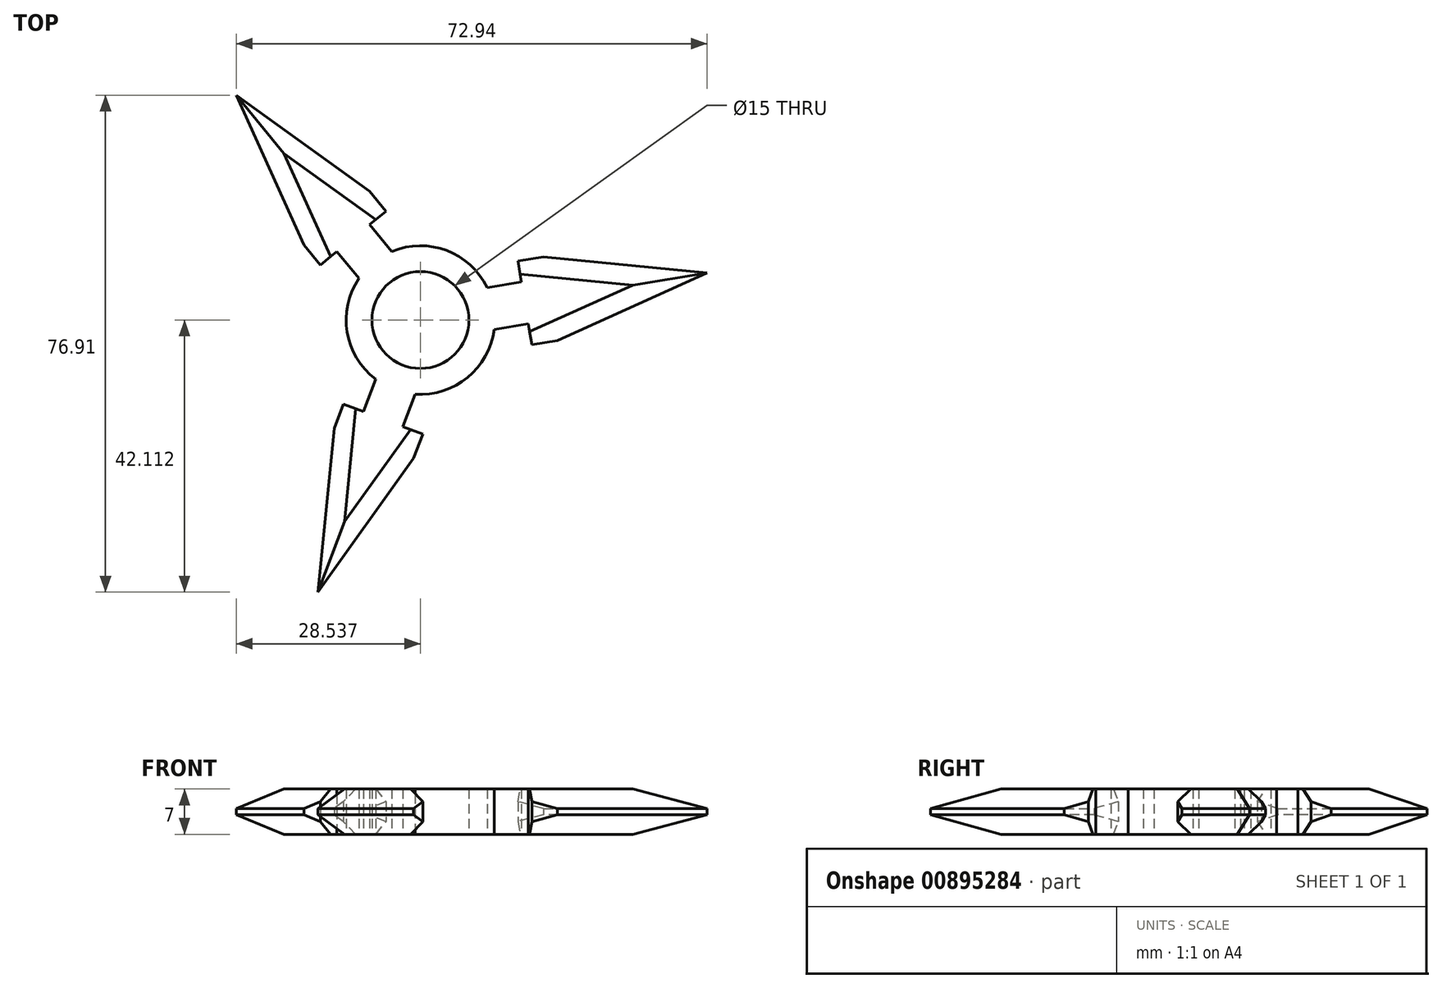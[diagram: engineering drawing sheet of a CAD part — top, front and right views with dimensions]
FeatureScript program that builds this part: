
annotation { "Feature Type Name" : "Feature", "Feature Type Description" : "" }
export const myFeature = defineFeature(function(context is Context, id is Id, definition is map)
    precondition{}
    {
        {
            var Q0;
            Q0=qCreatedBy(makeId("Top.planeOp"),FACE);
            var sketch = newSketch(context, id + "F0", { "sketchPlane" : qUnion([Q0])});
            skLineSegment(sketch, "E0", {"start": v(-19.22, 0.26) * mm, "end": v(-22.63, 4.41) * mm});
            skLineSegment(sketch, "E1", {"start": v(-22.63, 4.41) * mm, "end": v(-25.16, 2.34) * mm});
            skPoint(sketch, "E1.endSnap0", {"position": v(-20.92, 2.34) * mm});
            skLineSegment(sketch, "E2", {"start": v(-25.16, 2.34) * mm, "end": v(-27.7, 5.43) * mm});
            skLineSegment(sketch, "E3", {"start": v(-27.7, 5.43) * mm, "end": v(-38.23, 28.6) * mm});
            skLineSegment(sketch, "E4", {"start": v(-38.23, 28.6) * mm, "end": v(-17.56, 13.75) * mm});
            skLineSegment(sketch, "E5", {"start": v(-17.56, 13.75) * mm, "end": v(-15.02, 10.65) * mm});
            skLineSegment(sketch, "E6", {"start": v(-15.02, 10.65) * mm, "end": v(-17.56, 8.57) * mm});
            skLineSegment(sketch, "E7", {"start": v(-17.56, 8.57) * mm, "end": v(-14.15, 4.41) * mm});
            skCircle(sketch, "E8", {"center": v(-9.7, -6.19) * mm, "radius": 11.5 * mm});
            skLineSegment(sketch, "E9.1.0", {"start": v(-25.56, -48.3) * mm, "end": v(-23.03, -22.97) * mm});
            skLineSegment(sketch, "E9.1.1", {"start": v(-10.75, -27.6) * mm, "end": v(-25.56, -48.3) * mm});
            skLineSegment(sketch, "E9.1.2", {"start": v(-9.34, -23.85) * mm, "end": v(-10.75, -27.6) * mm});
            skLineSegment(sketch, "E9.1.3", {"start": v(-12.4, -22.7) * mm, "end": v(-9.34, -23.85) * mm});
            skLineSegment(sketch, "E9.1.4", {"start": v(-10.51, -17.66) * mm, "end": v(-12.4, -22.7) * mm});
            skLineSegment(sketch, "E9.1.5", {"start": v(-18.55, -20.38) * mm, "end": v(-16.65, -15.35) * mm});
            skLineSegment(sketch, "E9.1.6", {"start": v(-21.62, -19.22) * mm, "end": v(-18.55, -20.38) * mm});
            skLineSegment(sketch, "E9.1.7", {"start": v(-23.03, -22.97) * mm, "end": v(-21.62, -19.22) * mm});
            skLineSegment(sketch, "E9.2.0", {"start": v(34.7, 1.12) * mm, "end": v(11.5, -9.35) * mm});
            skLineSegment(sketch, "E9.2.1", {"start": v(9.37, 3.6) * mm, "end": v(34.7, 1.12) * mm});
            skLineSegment(sketch, "E9.2.2", {"start": v(5.42, 2.95) * mm, "end": v(9.37, 3.6) * mm});
            skLineSegment(sketch, "E9.2.3", {"start": v(5.96, -0.29) * mm, "end": v(5.42, 2.95) * mm});
            skLineSegment(sketch, "E9.2.4", {"start": v(0.65, -1.16) * mm, "end": v(5.96, -0.29) * mm});
            skLineSegment(sketch, "E9.2.5", {"start": v(7.02, -6.76) * mm, "end": v(1.72, -7.63) * mm});
            skLineSegment(sketch, "E9.2.6", {"start": v(7.56, -10) * mm, "end": v(7.02, -6.76) * mm});
            skLineSegment(sketch, "E9.2.7", {"start": v(11.5, -9.35) * mm, "end": v(7.56, -10) * mm});
            skLineSegment(sketch, "E10", {"start": v(-25.56, -48.3) * mm, "end": v(-9.7, -6.19) * mm, "construction": true});
            skCircle(sketch, "E11", {"center": v(-9.7, -6.19) * mm, "radius": 7.5 * mm});
            skCircle(sketch, "E12", {"center": v(-9.7, -6.19) * mm, "radius": 45 * mm, "construction": true});
            skSolve(sketch);
        }
        {
            var Q0;
            Q0=makeQuery(id+"F0.imprint","IMPRINT",FACE,{"disambiguationData":[TD([[makeQuery(id+"F0.imprint","IMPRINT",EDGE,{"derivedFrom":sQuery(id+"F0.wireOp",EDGE,"E9.1.0")}),-1.0]])]});
            var Q1;
            Q1=makeQuery(id+"F0.imprint","IMPRINT",FACE,{"disambiguationData":[TD([[makeQuery(id+"F0.imprint","IMPRINT",EDGE,{"derivedFrom":sQuery(id+"F0.wireOp",EDGE,"E9.2.0")}),-1.0]])]});
            var Q2;
            {var subQ0=sQuery(id+"F0.wireOp",EDGE,"E0");Q2=makeQuery(id+"F0.imprint","IMPRINT",FACE,{"disambiguationData":[TD([[makeQuery(id+"F0.imprint","IMPRINT",EDGE,{"derivedFrom":subQ0}),-1.0]])]});}
            var Q3;
            {var subQ5=sQuery(id+"F0.wireOp",EDGE,"E1");Q3=makeQuery(id+"F0.imprint","IMPRINT",FACE,{"disambiguationData":[TD([[makeQuery(id+"F0.imprint","IMPRINT",EDGE,{"derivedFrom":subQ5}),-1.0]])]});}
            var Q4;
            {var subQ0=sQuery(id+"F0.wireOp",EDGE,"E8");var subQ1=sQuery(id+"F0.wireOp",EDGE,"E7");var subQ2=makeQuery(id+"F0.imprint","INTERSECT",VERTEX,{"derivedFrom":[subQ1,subQ0]});Q4=makeQuery(id+"F0.imprint","IMPRINT",FACE,{"disambiguationData":[TD([[makeQuery(id+"F0.imprint","IMPRINT",EDGE,{"disambiguationData":[TD([[subQ2,1.0]])],"derivedFrom":subQ1}),1.0]])]});}
            var Q5;
            {var subQ0=sQuery(id+"F0.wireOp",EDGE,"E8");var subQ1=sQuery(id+"F0.wireOp",EDGE,"E0");var subQ2=makeQuery(id+"F0.imprint","INTERSECT",VERTEX,{"derivedFrom":[subQ1,subQ0]});Q5=makeQuery(id+"F0.imprint","IMPRINT",FACE,{"disambiguationData":[TD([[makeQuery(id+"F0.imprint","IMPRINT",EDGE,{"disambiguationData":[TD([[subQ2,-1.0]])],"derivedFrom":subQ1}),1.0]])]});}
            var Q6;
            {var subQ0=sQuery(id+"F0.wireOp",EDGE,"E9.1.4");var subQ1=sQuery(id+"F0.wireOp",EDGE,"E8");var subQ2=makeQuery(id+"F0.imprint","INTERSECT",VERTEX,{"derivedFrom":[subQ1,subQ0]});Q6=makeQuery(id+"F0.imprint","IMPRINT",FACE,{"disambiguationData":[TD([[makeQuery(id+"F0.imprint","IMPRINT",EDGE,{"disambiguationData":[TD([[subQ2,1.0]])],"derivedFrom":subQ1}),-1.0]])]});}
            var Q7;
            {var subQ0=sQuery(id+"F0.wireOp",EDGE,"E9.1.4");var subQ1=sQuery(id+"F0.wireOp",EDGE,"E8");var subQ2=makeQuery(id+"F0.imprint","INTERSECT",VERTEX,{"derivedFrom":[subQ1,subQ0]});Q7=makeQuery(id+"F0.imprint","IMPRINT",FACE,{"disambiguationData":[TD([[makeQuery(id+"F0.imprint","IMPRINT",EDGE,{"disambiguationData":[TD([[subQ2,-1.0]])],"derivedFrom":subQ1}),-1.0]])]});}
            var Q8;
            {var subQ0=sQuery(id+"F0.wireOp",EDGE,"E9.2.4");var subQ1=sQuery(id+"F0.wireOp",EDGE,"E8");var subQ2=makeQuery(id+"F0.imprint","INTERSECT",VERTEX,{"derivedFrom":[subQ1,subQ0]});Q8=makeQuery(id+"F0.imprint","IMPRINT",FACE,{"disambiguationData":[TD([[makeQuery(id+"F0.imprint","IMPRINT",EDGE,{"disambiguationData":[TD([[subQ2,1.0]])],"derivedFrom":subQ1}),-1.0]])]});}
            var Q9;
            Q9=makeQuery(id+"F0.imprint","IMPRINT",FACE,{"disambiguationData":[TD([[makeQuery(id+"F0.imprint","IMPRINT",EDGE,{"derivedFrom":sQuery(id+"F0.wireOp",EDGE,"E11")}),-1.0]])]});
            extrude(context, id + "F1", {"entities" : qUnion([Q0, Q1, Q2, Q3, Q4, Q5, Q6, Q7, Q8, Q9]), "depth" : 7 * mm, "offsetDistance" : 25 * mm});
        }
        {
            var Q0;
            Q0=makeQuery(id+"F1.opExtrude","CAP_EDGE",EDGE,{"disambiguationData":[OSD([sQuery(id+"F0.wireOp",EDGE,"E9.2.1")])],"isStart":true});
            var Q1;
            Q1=makeQuery(id+"F1.opExtrude","CAP_EDGE",EDGE,{"disambiguationData":[OSD([sQuery(id+"F0.wireOp",EDGE,"E9.2.0")])],"isStart":true});
            var Q2;
            Q2=makeQuery(id+"F1.opExtrude","CAP_EDGE",EDGE,{"disambiguationData":[OSD([sQuery(id+"F0.wireOp",EDGE,"E9.2.1")])],"isStart":false});
            var Q3;
            Q3=makeQuery(id+"F1.opExtrude","CAP_EDGE",EDGE,{"disambiguationData":[OSD([sQuery(id+"F0.wireOp",EDGE,"E9.1.1")])],"isStart":true});
            var Q4;
            Q4=makeQuery(id+"F1.opExtrude","CAP_EDGE",EDGE,{"disambiguationData":[OSD([sQuery(id+"F0.wireOp",EDGE,"E9.1.0")])],"isStart":true});
            var Q5;
            Q5=makeQuery(id+"F1.opExtrude","CAP_EDGE",EDGE,{"disambiguationData":[OSD([sQuery(id+"F0.wireOp",EDGE,"E3")])],"isStart":true});
            var Q6;
            Q6=makeQuery(id+"F1.opExtrude","CAP_EDGE",EDGE,{"disambiguationData":[OSD([sQuery(id+"F0.wireOp",EDGE,"E4")])],"isStart":true});
            var Q7;
            Q7=makeQuery(id+"F1.opExtrude","CAP_EDGE",EDGE,{"disambiguationData":[OSD([sQuery(id+"F0.wireOp",EDGE,"E9.1.1")])],"isStart":false});
            var Q8;
            Q8=makeQuery(id+"F1.opExtrude","CAP_EDGE",EDGE,{"disambiguationData":[OSD([sQuery(id+"F0.wireOp",EDGE,"E9.1.0")])],"isStart":false});
            var Q9;
            Q9=makeQuery(id+"F1.opExtrude","CAP_EDGE",EDGE,{"disambiguationData":[OSD([sQuery(id+"F0.wireOp",EDGE,"E9.2.0")])],"isStart":false});
            var Q10;
            Q10=makeQuery(id+"F1.opExtrude","CAP_EDGE",EDGE,{"disambiguationData":[OSD([sQuery(id+"F0.wireOp",EDGE,"E4")])],"isStart":false});
            var Q11;
            Q11=makeQuery(id+"F1.opExtrude","CAP_EDGE",EDGE,{"disambiguationData":[OSD([sQuery(id+"F0.wireOp",EDGE,"E3")])],"isStart":false});
            chamfer(context, id + "F2", {"entities" : qUnion([Q0, Q1, Q2, Q3, Q4, Q5, Q6, Q7, Q8, Q9, Q10, Q11]), "width" : 3 * mm, "tangentPropagation" : true});
        }
    });
